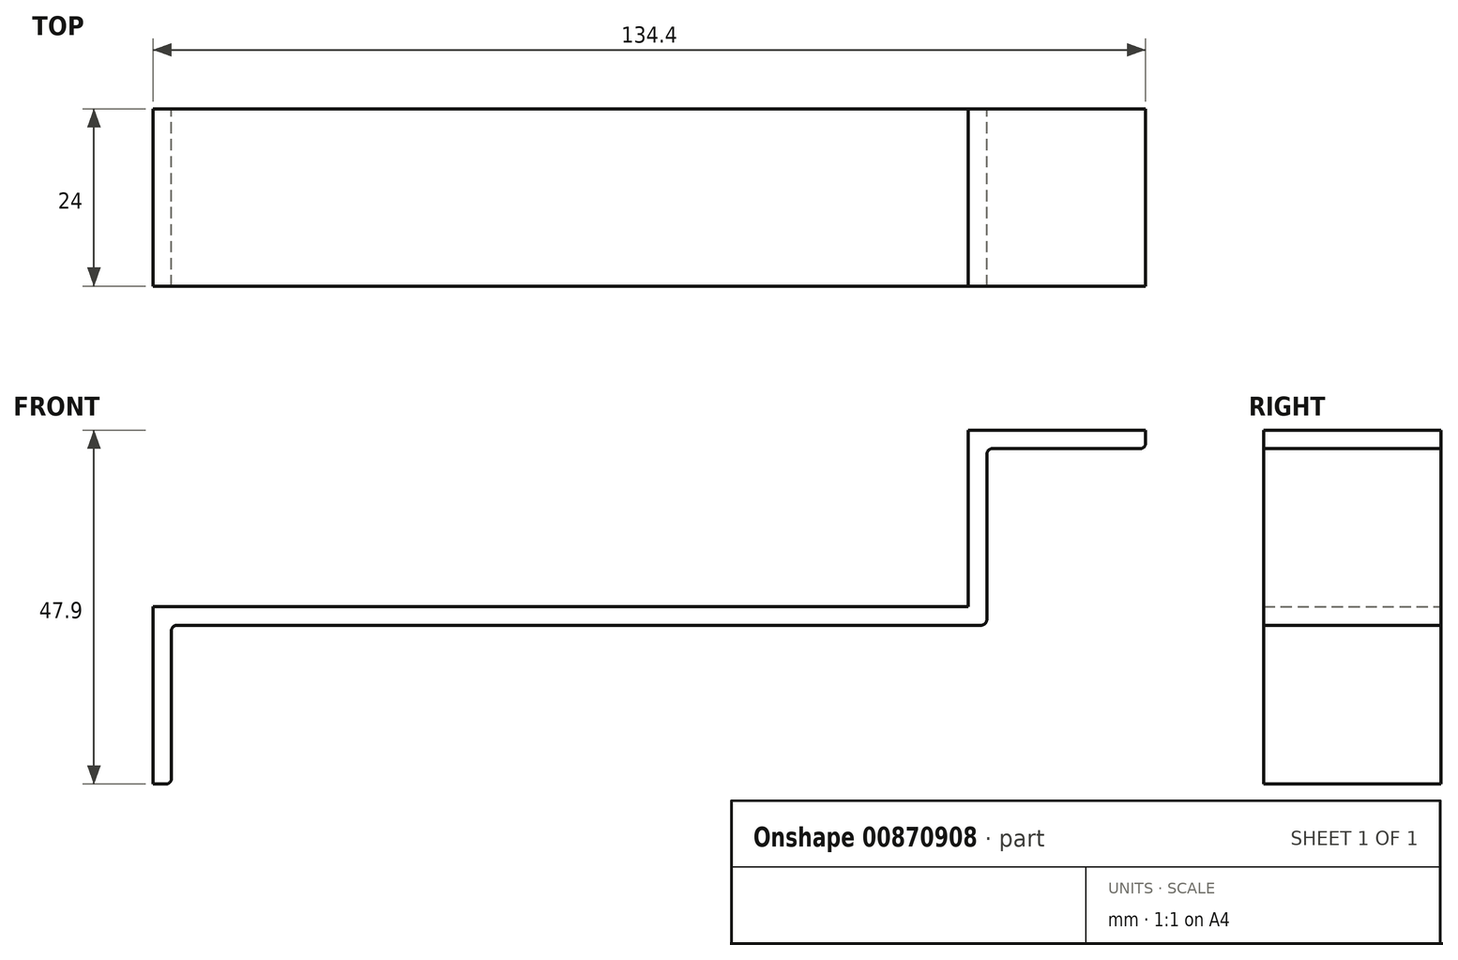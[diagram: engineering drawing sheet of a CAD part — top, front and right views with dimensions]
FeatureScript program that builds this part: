
annotation { "Feature Type Name" : "Feature", "Feature Type Description" : "" }
export const myFeature = defineFeature(function(context is Context, id is Id, definition is map)
    precondition{}
    {
        {
            var Q0;
            Q0=qCreatedBy(makeId("Front.planeOp"),FACE);
            var sketch = newSketch(context, id + "F0", { "sketchPlane" : qUnion([Q0])});
            skLineSegment(sketch, "E0.bottom", {"start": v(-55.2, 11.95) * mm, "end": v(55.2, 11.95) * mm, "construction": true});
            skLineSegment(sketch, "E0.top", {"start": v(-55.2, -11.95) * mm, "end": v(55.2, -11.95) * mm, "construction": true});
            skLineSegment(sketch, "E0.left", {"start": v(-55.2, 11.95) * mm, "end": v(-55.2, -11.95) * mm, "construction": true});
            skLineSegment(sketch, "E0.right", {"start": v(55.2, 11.95) * mm, "end": v(55.2, -11.95) * mm, "construction": true});
            skLineSegment(sketch, "E1", {"start": v(-55.2, 0) * mm, "end": v(55.2, 0) * mm, "construction": true});
            skLineSegment(sketch, "E2.bottom", {"start": v(-55.2, -11.95) * mm, "end": v(57.7, -11.95) * mm});
            skLineSegment(sketch, "E2.top", {"start": v(-51.94, -14.45) * mm, "end": v(56.94, -14.45) * mm});
            skLineSegment(sketch, "E2.left", {"start": v(-55.2, -11.95) * mm, "end": v(-55.2, -14.45) * mm});
            skLineSegment(sketch, "E2.right", {"start": v(57.7, -11.95) * mm, "end": v(57.7, -13.7) * mm});
            skLineSegment(sketch, "E3.bottom", {"start": v(-55.2, -14.45) * mm, "end": v(-52.7, -14.45) * mm});
            skLineSegment(sketch, "E3.top", {"start": v(-55.2, -35.95) * mm, "end": v(-53.46, -35.95) * mm});
            skLineSegment(sketch, "E3.left", {"start": v(-55.2, -14.45) * mm, "end": v(-55.2, -35.95) * mm});
            skLineSegment(sketch, "E3.right", {"start": v(-52.7, -15.2) * mm, "end": v(-52.7, -35.2) * mm});
            skLineSegment(sketch, "E4.bottom", {"start": v(57.7, -11.95) * mm, "end": v(55.2, -11.95) * mm});
            skLineSegment(sketch, "E4.top", {"start": v(57.7, 11.95) * mm, "end": v(55.2, 11.95) * mm});
            skLineSegment(sketch, "E4.left", {"start": v(57.7, -11.95) * mm, "end": v(57.7, 8.7) * mm});
            skLineSegment(sketch, "E4.right", {"start": v(55.2, -11.95) * mm, "end": v(55.2, 11.95) * mm});
            skLineSegment(sketch, "E5.bottom", {"start": v(57.7, 11.95) * mm, "end": v(79.2, 11.95) * mm});
            skLineSegment(sketch, "E5.top", {"start": v(58.46, 9.45) * mm, "end": v(78.44, 9.45) * mm});
            skLineSegment(sketch, "E5.left", {"start": v(57.7, 11.95) * mm, "end": v(57.7, 9.45) * mm});
            skLineSegment(sketch, "E5.right", {"start": v(79.2, 11.95) * mm, "end": v(79.2, 10.2) * mm});
            skPoint(sketch, "E6.visualSharp", {"position": v(57.7, -14.45) * mm});
            skArc(sketch, "E6.filletArc", {"start": v(56.94, -14.45) * mm, "mid": v(57.48, -14.23) * mm, "end": v(57.7, -13.7) * mm});
            skArc(sketch, "E7.filletArc", {"start": v(58.46, 9.45) * mm, "mid": v(57.92, 9.23) * mm, "end": v(57.7, 8.7) * mm});
            skArc(sketch, "E8.filletArc", {"start": v(-51.94, -14.45) * mm, "mid": v(-52.48, -14.67) * mm, "end": v(-52.7, -15.2) * mm});
            skPoint(sketch, "E9.visualSharp", {"position": v(-52.7, -35.95) * mm});
            skArc(sketch, "E9.filletArc", {"start": v(-53.46, -35.95) * mm, "mid": v(-52.92, -35.73) * mm, "end": v(-52.7, -35.2) * mm});
            skPoint(sketch, "E10.visualSharp", {"position": v(79.2, 9.45) * mm});
            skArc(sketch, "E10.filletArc", {"start": v(78.44, 9.45) * mm, "mid": v(78.98, 9.67) * mm, "end": v(79.2, 10.2) * mm});
            skSolve(sketch);
        }
        {
            var Q0;
            Q0 = qSketchRegion(id + "F0", true);
            extrude(context, id + "F1", {"entities" : qUnion([Q0]), "depth" : 24 * mm, "offsetDistance" : 25 * mm});
        }
    });
